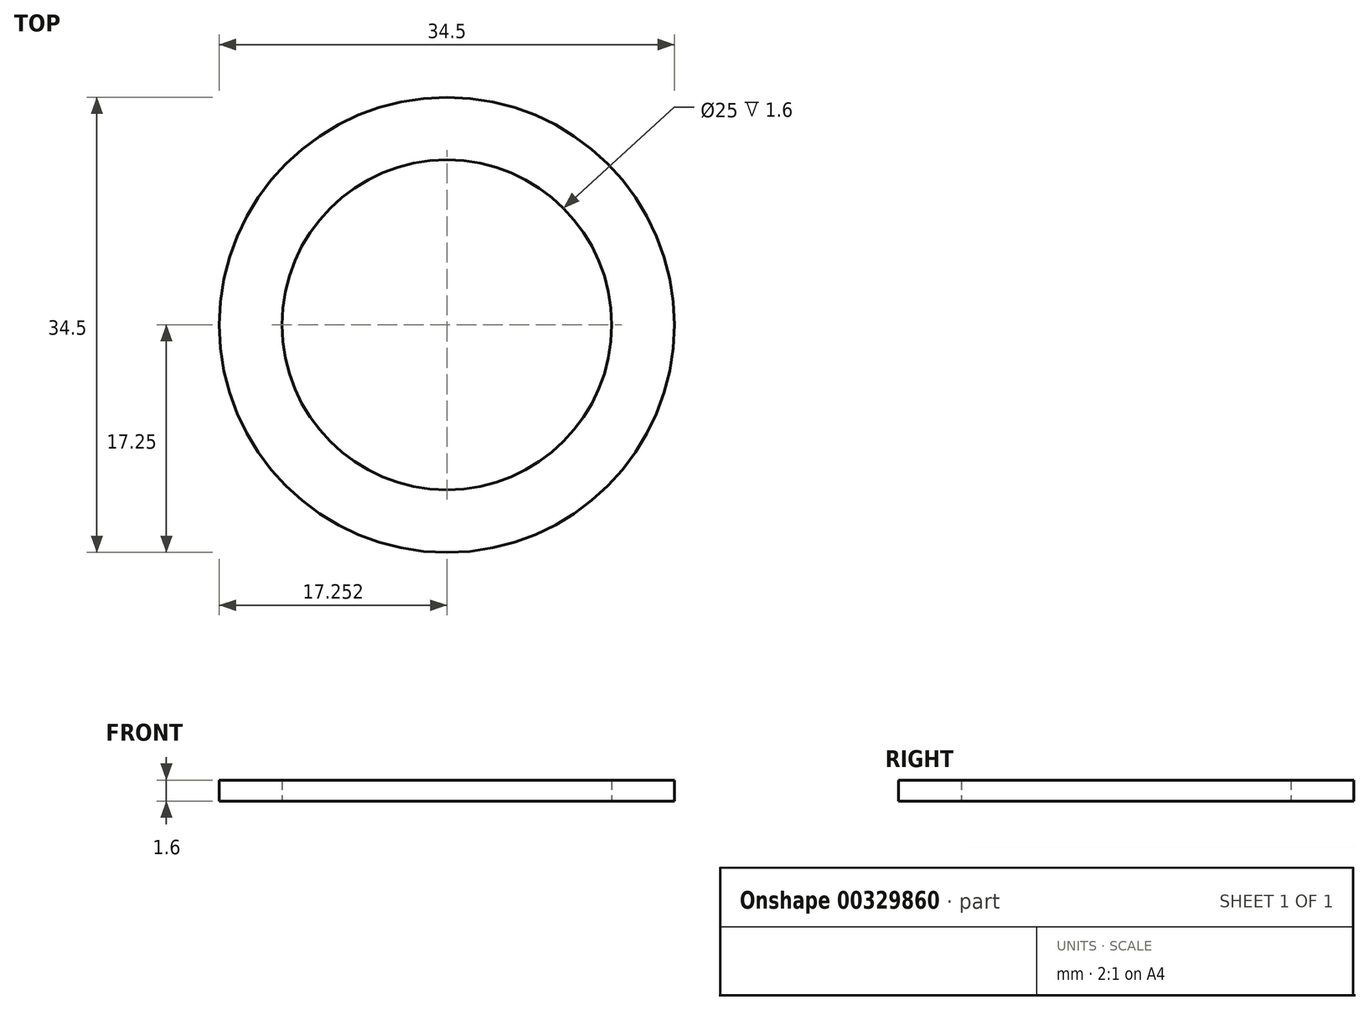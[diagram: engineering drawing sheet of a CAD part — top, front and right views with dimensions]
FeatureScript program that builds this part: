
annotation { "Feature Type Name" : "Feature", "Feature Type Description" : "" }
export const myFeature = defineFeature(function(context is Context, id is Id, definition is map)
    precondition{}
    {
        {
            var Q0;
            Q0=qCreatedBy(makeId("Top.planeOp"),FACE);
            var sketch = newSketch(context, id + "F0", { "sketchPlane" : qUnion([Q0])});
            skArc(sketch, "E0", {"start": v(-6.5, 16.25) * mm, "mid": v(-16.9, 4.53) * mm, "end": v(-13.75, -10.82) * mm});
            skLineSegment(sketch, "E1", {"start": v(-6.5, 16.25) * mm, "end": v(-6.5, 19.2) * mm});
            skLineSegment(sketch, "E2", {"start": v(-6.5, 19.2) * mm, "end": v(6.5, 19.2) * mm});
            skLineSegment(sketch, "E3", {"start": v(6.5, 19.2) * mm, "end": v(6.5, 16.25) * mm});
            skLineSegment(sketch, "E4", {"start": v(0, 19.2) * mm, "end": v(0, 0) * mm, "construction": true});
            skLineSegment(sketch, "E5.1.0", {"start": v(-2.5, -17.32) * mm, "end": v(-3.97, -19.88) * mm});
            skLineSegment(sketch, "E5.1.1", {"start": v(-3.97, -19.88) * mm, "end": v(-15.23, -13.38) * mm});
            skLineSegment(sketch, "E5.1.2", {"start": v(-15.23, -13.38) * mm, "end": v(-13.75, -10.82) * mm});
            skLineSegment(sketch, "E6", {"start": v(-9.6, -16.63) * mm, "end": v(0, 0) * mm, "construction": true});
            skArc(sketch, "E7.trimOffspring", {"start": v(-2.5, -17.32) * mm, "mid": v(16.9, -4.53) * mm, "end": v(6.5, 16.25) * mm});
            skCircle(sketch, "E8", {"center": v(0, 0) * mm, "radius": 24.55 * mm});
            skCircle(sketch, "E9", {"center": v(85, 0) * mm, "radius": 12.5 * mm});
            skCircle(sketch, "E10", {"center": v(85, 0) * mm, "radius": 17.25 * mm});
            skSolve(sketch);
        }
        {
            var Q0;
            Q0=makeQuery(id+"F0.imprint","IMPRINT",FACE,{"disambiguationData":[TD([[makeQuery(id+"F0.imprint","IMPRINT",EDGE,{"derivedFrom":sQuery(id+"F0.wireOp",EDGE,"E9")}),-1.0]])]});
            extrude(context, id + "F1", {"entities" : qUnion([Q0]), "depth" : 1.6 * mm, "offsetDistance" : 25 * mm});
        }
    });
